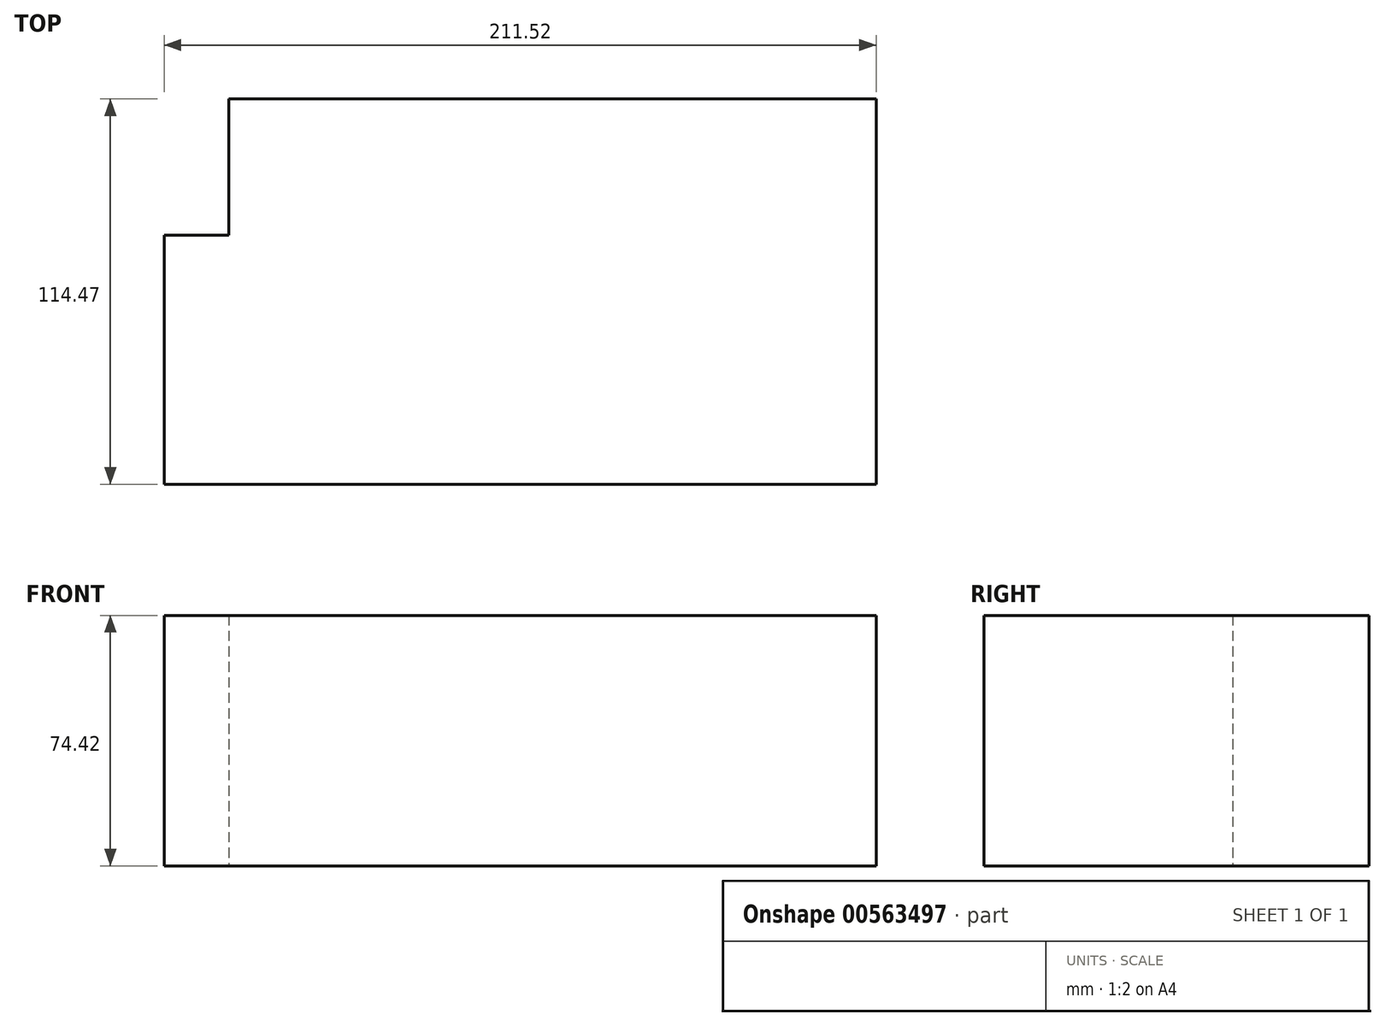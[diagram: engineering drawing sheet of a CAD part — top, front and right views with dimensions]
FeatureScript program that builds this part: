
annotation { "Feature Type Name" : "Feature", "Feature Type Description" : "" }
export const myFeature = defineFeature(function(context is Context, id is Id, definition is map)
    precondition{}
    {
        {
            var Q0;
            Q0=qCreatedBy(makeId("Top.planeOp"),FACE);
            var sketch = newSketch(context, id + "F0", { "sketchPlane" : qUnion([Q0])});
            skLineSegment(sketch, "E0.bottom", {"start": v(-125.81, 0) * mm, "end": v(66.56, 0) * mm});
            skLineSegment(sketch, "E0.top", {"start": v(-125.81, -114.47) * mm, "end": v(66.56, -114.47) * mm});
            skLineSegment(sketch, "E0.left", {"start": v(-125.81, 0) * mm, "end": v(-125.81, -114.47) * mm});
            skLineSegment(sketch, "E0.right", {"start": v(66.56, 0) * mm, "end": v(66.56, -114.47) * mm});
            skLineSegment(sketch, "E1.bottom", {"start": v(-125.81, -114.47) * mm, "end": v(-144.96, -114.47) * mm});
            skLineSegment(sketch, "E1.top", {"start": v(-125.81, -40.44) * mm, "end": v(-144.96, -40.44) * mm});
            skLineSegment(sketch, "E1.left", {"start": v(-125.81, -114.47) * mm, "end": v(-125.81, -40.44) * mm});
            skLineSegment(sketch, "E1.right", {"start": v(-144.96, -114.47) * mm, "end": v(-144.96, -40.44) * mm});
            skSolve(sketch);
        }
        {
            var Q0;
            Q0 = qSketchRegion(id + "F0", true);
            extrude(context, id + "F1", {"entities" : qUnion([Q0]), "depth" : 74.42 * mm, "offsetDistance" : 25.4 * mm});
        }
    });
